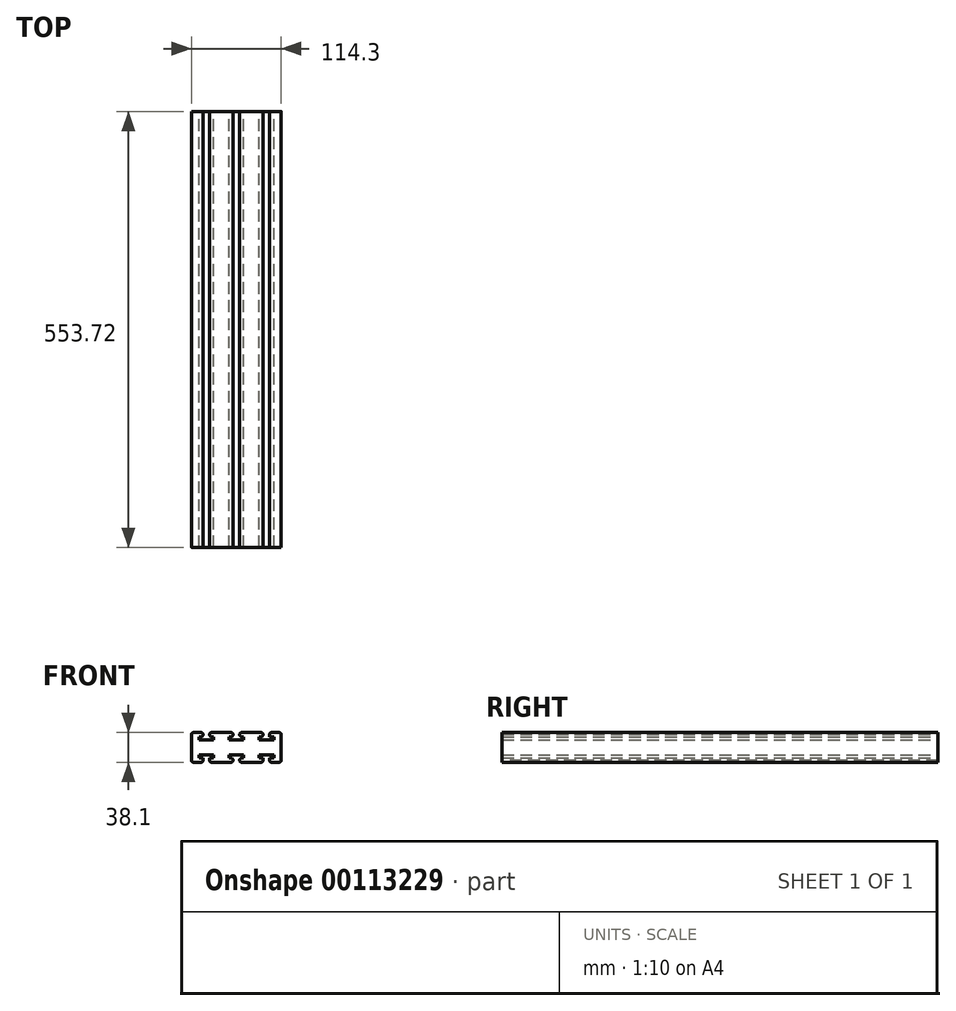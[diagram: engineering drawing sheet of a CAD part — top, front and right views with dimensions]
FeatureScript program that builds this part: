
annotation { "Feature Type Name" : "Feature", "Feature Type Description" : "" }
export const myFeature = defineFeature(function(context is Context, id is Id, definition is map)
    precondition{}
    {
        {
            var Q0;
            Q0=qCreatedBy(makeId("Front.planeOp"),FACE);
            var sketch = newSketch(context, id + "F0", { "sketchPlane" : qUnion([Q0])});
            skLineSegment(sketch, "E0.bottom", {"start": v(-57.15, 19.05) * mm, "end": v(57.15, 19.05) * mm});
            skLineSegment(sketch, "E0.top", {"start": v(-57.15, -19.05) * mm, "end": v(57.15, -19.05) * mm});
            skLineSegment(sketch, "E0.left", {"start": v(-57.15, 19.05) * mm, "end": v(-57.15, -19.05) * mm});
            skLineSegment(sketch, "E0.right", {"start": v(57.15, 19.05) * mm, "end": v(57.15, -19.05) * mm});
            skPoint(sketch, "E0.middle", {"position": v(0, 0) * mm});
            skLineSegment(sketch, "E1", {"start": v(-57.15, 19.05) * mm, "end": v(-19.05, 19.05) * mm});
            skLineSegment(sketch, "E2", {"start": v(0, -19.05) * mm, "end": v(0, 19.05) * mm});
            skLineSegment(sketch, "E3.bottom", {"start": v(-19.05, 19.05) * mm, "end": v(-17.88, 19.05) * mm});
            skLineSegment(sketch, "E4.bottom", {"start": v(-19.05, 19.05) * mm, "end": v(19.05, 19.05) * mm});
            skLineSegment(sketch, "E4.top", {"start": v(-19.05, -19.05) * mm, "end": v(19.05, -19.05) * mm});
            skLineSegment(sketch, "E5", {"start": v(-57.15, 19.05) * mm, "end": v(-38.1, 19.05) * mm});
            skLineSegment(sketch, "E6", {"start": v(-38.1, 19.05) * mm, "end": v(-38.1, -19.05) * mm});
            skLineSegment(sketch, "E7", {"start": v(19.05, 19.05) * mm, "end": v(38.1, 19.05) * mm});
            skLineSegment(sketch, "E8", {"start": v(38.1, 19.05) * mm, "end": v(38.1, -19.05) * mm});
            skLineSegment(sketch, "E9.bottom", {"start": v(34.1, 28.58) * mm, "end": v(42.1, 28.58) * mm});
            skLineSegment(sketch, "E9.top", {"start": v(34.1, 9.53) * mm, "end": v(42.1, 9.53) * mm});
            skLineSegment(sketch, "E9.left", {"start": v(34.1, 28.58) * mm, "end": v(34.1, 9.53) * mm});
            skLineSegment(sketch, "E9.right", {"start": v(42.1, 28.58) * mm, "end": v(42.1, 9.53) * mm});
            skPoint(sketch, "E9.middle", {"position": v(38.1, 19.05) * mm});
            skLineSegment(sketch, "E10.bottom", {"start": v(42.1, -9.52) * mm, "end": v(34.1, -9.52) * mm});
            skLineSegment(sketch, "E10.top", {"start": v(42.1, -28.57) * mm, "end": v(34.1, -28.57) * mm});
            skLineSegment(sketch, "E10.left", {"start": v(42.1, -9.52) * mm, "end": v(42.1, -28.57) * mm});
            skLineSegment(sketch, "E10.right", {"start": v(34.1, -9.52) * mm, "end": v(34.1, -28.57) * mm});
            skPoint(sketch, "E10.middle", {"position": v(38.1, -19.05) * mm});
            skLineSegment(sketch, "E11.bottom", {"start": v(4, -9.52) * mm, "end": v(-4, -9.52) * mm});
            skLineSegment(sketch, "E11.top", {"start": v(4, -28.57) * mm, "end": v(-4, -28.57) * mm});
            skLineSegment(sketch, "E11.left", {"start": v(4, -9.52) * mm, "end": v(4, -28.57) * mm});
            skLineSegment(sketch, "E11.right", {"start": v(-4, -9.52) * mm, "end": v(-4, -28.57) * mm});
            skPoint(sketch, "E11.middle", {"position": v(0, -19.05) * mm});
            skLineSegment(sketch, "E12.bottom", {"start": v(4, 28.58) * mm, "end": v(-4, 28.58) * mm});
            skLineSegment(sketch, "E12.top", {"start": v(4, 9.53) * mm, "end": v(-4, 9.53) * mm});
            skLineSegment(sketch, "E12.left", {"start": v(4, 28.58) * mm, "end": v(4, 9.53) * mm});
            skLineSegment(sketch, "E12.right", {"start": v(-4, 28.58) * mm, "end": v(-4, 9.53) * mm});
            skPoint(sketch, "E12.middle", {"position": v(0, 19.05) * mm});
            skLineSegment(sketch, "E13.bottom", {"start": v(-34.1, 28.58) * mm, "end": v(-42.1, 28.58) * mm});
            skLineSegment(sketch, "E13.top", {"start": v(-34.1, 9.53) * mm, "end": v(-42.1, 9.53) * mm});
            skLineSegment(sketch, "E13.left", {"start": v(-34.1, 28.58) * mm, "end": v(-34.1, 9.53) * mm});
            skLineSegment(sketch, "E13.right", {"start": v(-42.1, 28.58) * mm, "end": v(-42.1, 9.53) * mm});
            skPoint(sketch, "E13.middle", {"position": v(-38.1, 19.05) * mm});
            skLineSegment(sketch, "E14.bottom", {"start": v(-34.1, -9.52) * mm, "end": v(-42.1, -9.52) * mm});
            skLineSegment(sketch, "E14.top", {"start": v(-34.1, -28.57) * mm, "end": v(-42.1, -28.57) * mm});
            skLineSegment(sketch, "E14.left", {"start": v(-34.1, -9.52) * mm, "end": v(-34.1, -28.57) * mm});
            skLineSegment(sketch, "E14.right", {"start": v(-42.1, -9.52) * mm, "end": v(-42.1, -28.57) * mm});
            skPoint(sketch, "E14.middle", {"position": v(-38.1, -19.05) * mm});
            skLineSegment(sketch, "E15.top", {"start": v(-28.57, -13.53) * mm, "end": v(-47.62, -13.53) * mm});
            skPoint(sketch, "E15.middle", {"position": v(-38.1, -9.52) * mm});
            skLineSegment(sketch, "E16.bottom", {"start": v(-28.58, 13.53) * mm, "end": v(-47.63, 13.53) * mm});
            skPoint(sketch, "E16.middle", {"position": v(-38.1, 9.53) * mm});
            skPoint(sketch, "E17.endSnap0", {"position": v(38.1, 9.53) * mm});
            skLineSegment(sketch, "E18.bottom", {"start": v(-47.63, 13.53) * mm, "end": v(-28.58, 13.53) * mm});
            skLineSegment(sketch, "E18.top", {"start": v(-47.63, 9.53) * mm, "end": v(-28.58, 9.53) * mm});
            skLineSegment(sketch, "E18.left", {"start": v(-47.63, 13.53) * mm, "end": v(-47.63, 9.53) * mm});
            skLineSegment(sketch, "E18.right", {"start": v(-28.58, 13.53) * mm, "end": v(-28.58, 9.53) * mm});
            skLineSegment(sketch, "E19.bottom", {"start": v(-47.62, -13.53) * mm, "end": v(-28.57, -13.53) * mm});
            skLineSegment(sketch, "E19.top", {"start": v(-47.62, -9.52) * mm, "end": v(-28.57, -9.52) * mm});
            skLineSegment(sketch, "E19.left", {"start": v(-47.62, -13.53) * mm, "end": v(-47.62, -9.52) * mm});
            skLineSegment(sketch, "E19.right", {"start": v(-28.57, -13.53) * mm, "end": v(-28.57, -9.52) * mm});
            skLineSegment(sketch, "E20.bottom", {"start": v(-9.53, 13.53) * mm, "end": v(9.53, 13.53) * mm});
            skPoint(sketch, "E20.middle", {"position": v(0, 9.53) * mm});
            skLineSegment(sketch, "E21.top", {"start": v(9.53, -13.53) * mm, "end": v(-9.53, -13.53) * mm});
            skPoint(sketch, "E21.middle", {"position": v(0, -9.52) * mm});
            skLineSegment(sketch, "E22.bottom", {"start": v(28.57, 13.53) * mm, "end": v(47.62, 13.53) * mm});
            skLineSegment(sketch, "E23.top", {"start": v(28.57, -13.53) * mm, "end": v(47.62, -13.53) * mm});
            skPoint(sketch, "E23.middle", {"position": v(38.1, -9.52) * mm});
            skLineSegment(sketch, "E24.top", {"start": v(-9.53, 9.53) * mm, "end": v(9.53, 9.53) * mm});
            skLineSegment(sketch, "E24.left", {"start": v(-9.53, 13.53) * mm, "end": v(-9.53, 9.53) * mm});
            skLineSegment(sketch, "E24.right", {"start": v(9.53, 13.53) * mm, "end": v(9.53, 9.53) * mm});
            skLineSegment(sketch, "E25.top", {"start": v(9.53, -9.52) * mm, "end": v(-9.53, -9.52) * mm});
            skLineSegment(sketch, "E25.left", {"start": v(9.53, -13.53) * mm, "end": v(9.53, -9.52) * mm});
            skLineSegment(sketch, "E25.right", {"start": v(-9.53, -13.53) * mm, "end": v(-9.53, -9.52) * mm});
            skLineSegment(sketch, "E26.top", {"start": v(28.57, -9.52) * mm, "end": v(47.62, -9.52) * mm});
            skLineSegment(sketch, "E26.left", {"start": v(28.57, -13.53) * mm, "end": v(28.57, -9.52) * mm});
            skLineSegment(sketch, "E26.right", {"start": v(47.62, -13.53) * mm, "end": v(47.62, -9.52) * mm});
            skLineSegment(sketch, "E27.top", {"start": v(28.57, 9.53) * mm, "end": v(47.62, 9.53) * mm});
            skLineSegment(sketch, "E27.left", {"start": v(28.57, 13.53) * mm, "end": v(28.57, 9.53) * mm});
            skLineSegment(sketch, "E27.right", {"start": v(47.62, 13.53) * mm, "end": v(47.62, 9.53) * mm});
            skSolve(sketch);
        }
        {
            var Q0;
            {var subQ1=sQuery(id+"F0.wireOp",EDGE,"E0.right");Q0=makeQuery(id+"F0.imprint","IMPRINT",FACE,{"disambiguationData":[TD([[makeQuery(id+"F0.imprint","IMPRINT",EDGE,{"derivedFrom":subQ1}),-1.0]])]});}
            var Q1;
            {var subQ15=sQuery(id+"F0.wireOp",EDGE,"E0.left");Q1=makeQuery(id+"F0.imprint","IMPRINT",FACE,{"disambiguationData":[TD([[makeQuery(id+"F0.imprint","IMPRINT",EDGE,{"derivedFrom":subQ15}),1.0]])]});}
            var Q2;
            {var subQ20=sQuery(id+"F0.wireOp",EDGE,"E18.right");Q2=makeQuery(id+"F0.imprint","IMPRINT",FACE,{"disambiguationData":[TD([[makeQuery(id+"F0.imprint","IMPRINT",EDGE,{"derivedFrom":subQ20}),1.0]])]});}
            var Q3;
            {var subQ12=sQuery(id+"F0.wireOp",EDGE,"E24.right");Q3=makeQuery(id+"F0.imprint","IMPRINT",FACE,{"disambiguationData":[TD([[makeQuery(id+"F0.imprint","IMPRINT",EDGE,{"derivedFrom":subQ12}),1.0]])]});}
            extrude(context, id + "F1", {"entities" : qUnion([Q0, Q1, Q2, Q3]), "depth" : 553.72 * mm});
        }
        {
            var Q0;
            Q0=makeQuery(id+"F1.opExtrude","SWEPT_EDGE",EDGE,{"disambiguationData":[OSD([sQuery(id+"F0.wireOp",EDGE,"E4.top"),sQuery(id+"F0.wireOp",EDGE,"E11.left")])]});
            var Q1;
            Q1=makeQuery(id+"F1.opExtrude","SWEPT_EDGE",EDGE,{"disambiguationData":[OSD([sQuery(id+"F0.wireOp",EDGE,"E0.top"),sQuery(id+"F0.wireOp",EDGE,"E10.right")])]});
            var Q2;
            Q2=makeQuery(id+"F1.opExtrude","SWEPT_EDGE",EDGE,{"disambiguationData":[OSD([sQuery(id+"F0.wireOp",EDGE,"E0.top"),sQuery(id+"F0.wireOp",EDGE,"E10.left")])]});
            var Q3;
            Q3=makeQuery(id+"F1.opExtrude","SWEPT_EDGE",EDGE,{"disambiguationData":[OSD([sQuery(id+"F0.wireOp",EDGE,"E0.top"),sQuery(id+"F0.wireOp",EDGE,"E0.right")])]});
            var Q4;
            Q4=makeQuery(id+"F1.opExtrude","SWEPT_EDGE",EDGE,{"disambiguationData":[OSD([sQuery(id+"F0.wireOp",EDGE,"E4.top"),sQuery(id+"F0.wireOp",EDGE,"E11.right")])]});
            var Q5;
            Q5=makeQuery(id+"F1.opExtrude","SWEPT_EDGE",EDGE,{"disambiguationData":[OSD([sQuery(id+"F0.wireOp",EDGE,"E0.top"),sQuery(id+"F0.wireOp",EDGE,"E14.left")])]});
            var Q6;
            Q6=makeQuery(id+"F1.opExtrude","SWEPT_EDGE",EDGE,{"disambiguationData":[OSD([sQuery(id+"F0.wireOp",EDGE,"E0.top"),sQuery(id+"F0.wireOp",EDGE,"E14.right")])]});
            var Q7;
            Q7=makeQuery(id+"F1.opExtrude","SWEPT_EDGE",EDGE,{"disambiguationData":[OSD([sQuery(id+"F0.wireOp",EDGE,"E0.top"),sQuery(id+"F0.wireOp",EDGE,"E0.left")])]});
            var Q8;
            Q8=makeQuery(id+"F1.opExtrude","SWEPT_EDGE",EDGE,{"disambiguationData":[OSD([sQuery(id+"F0.wireOp",EDGE,"E0.left"),sQuery(id+"F0.wireOp",EDGE,"E5")])]});
            var Q9;
            Q9=makeQuery(id+"F1.opExtrude","SWEPT_EDGE",EDGE,{"disambiguationData":[OSD([sQuery(id+"F0.wireOp",EDGE,"E5"),sQuery(id+"F0.wireOp",EDGE,"E13.right")])]});
            var Q10;
            Q10=makeQuery(id+"F1.opExtrude","SWEPT_EDGE",EDGE,{"disambiguationData":[OSD([sQuery(id+"F0.wireOp",EDGE,"E1"),sQuery(id+"F0.wireOp",EDGE,"E13.left")])]});
            var Q11;
            Q11=makeQuery(id+"F1.opExtrude","SWEPT_EDGE",EDGE,{"disambiguationData":[OSD([sQuery(id+"F0.wireOp",EDGE,"E4.bottom"),sQuery(id+"F0.wireOp",EDGE,"E12.right")])]});
            var Q12;
            Q12=makeQuery(id+"F1.opExtrude","SWEPT_EDGE",EDGE,{"disambiguationData":[OSD([sQuery(id+"F0.wireOp",EDGE,"E4.bottom"),sQuery(id+"F0.wireOp",EDGE,"E12.left")])]});
            var Q13;
            Q13=makeQuery(id+"F1.opExtrude","SWEPT_EDGE",EDGE,{"disambiguationData":[OSD([sQuery(id+"F0.wireOp",EDGE,"E7"),sQuery(id+"F0.wireOp",EDGE,"E9.left")])]});
            var Q14;
            Q14=makeQuery(id+"F1.opExtrude","SWEPT_EDGE",EDGE,{"disambiguationData":[OSD([sQuery(id+"F0.wireOp",EDGE,"E0.bottom"),sQuery(id+"F0.wireOp",EDGE,"E9.right")])]});
            var Q15;
            Q15=makeQuery(id+"F1.opExtrude","SWEPT_EDGE",EDGE,{"disambiguationData":[OSD([sQuery(id+"F0.wireOp",EDGE,"E0.bottom"),sQuery(id+"F0.wireOp",EDGE,"E0.right")])]});
            fillet(context, id + "F2", {"entities" : qUnion([Q0, Q1, Q2, Q3, Q4, Q5, Q6, Q7, Q8, Q9, Q10, Q11, Q12, Q13, Q14, Q15]), "radius" : 3.17 * mm, "tangentPropagation" : true, "allowEdgeOverflow" : false});
        }
    });
